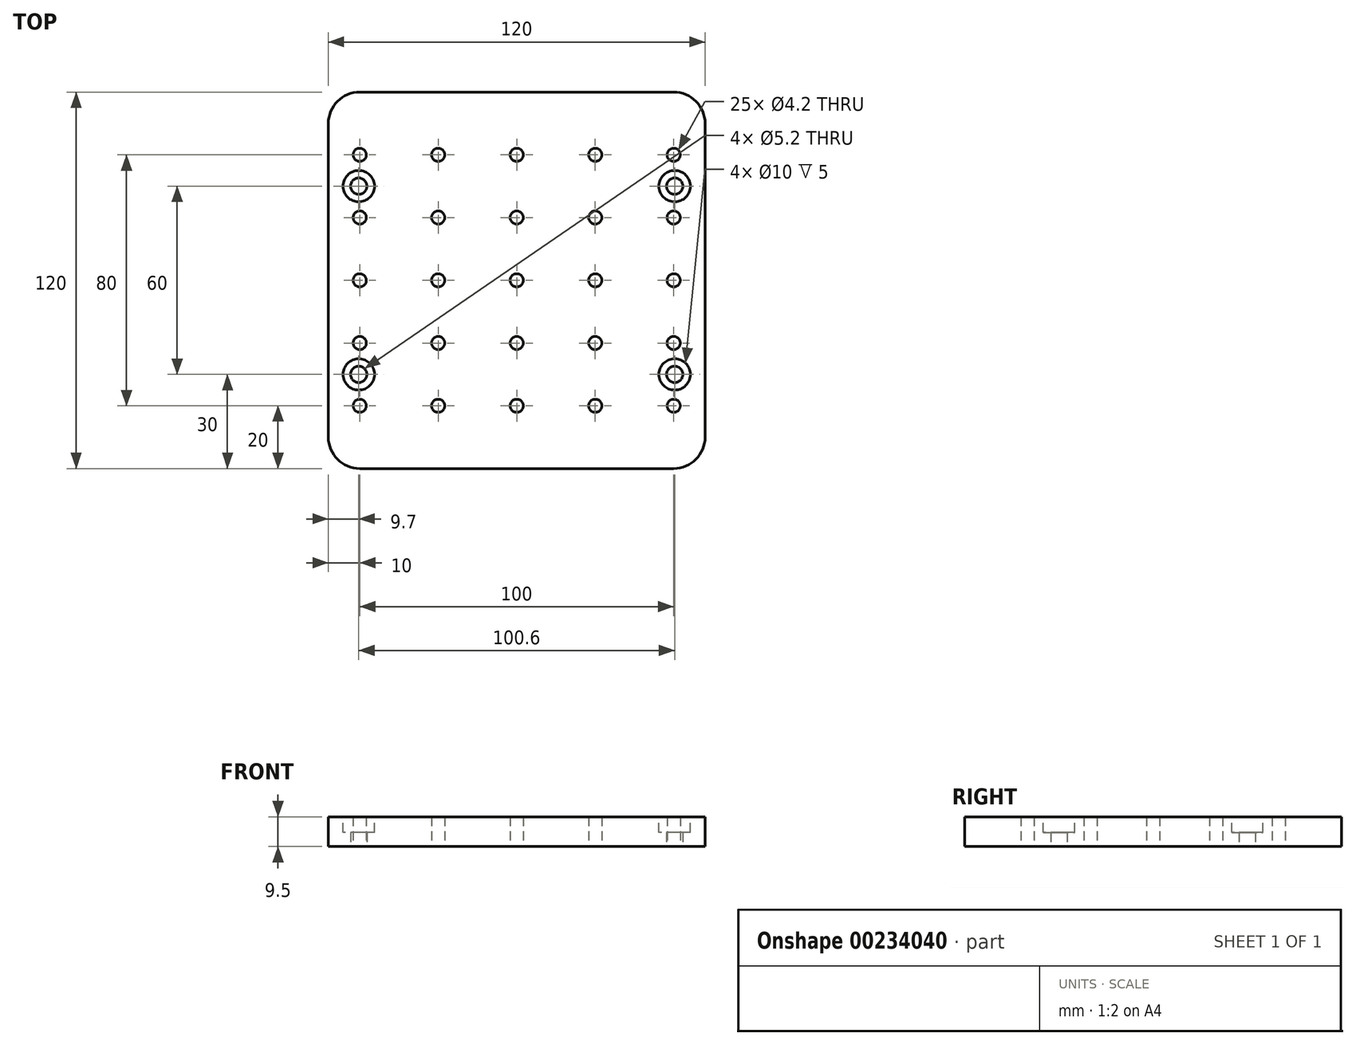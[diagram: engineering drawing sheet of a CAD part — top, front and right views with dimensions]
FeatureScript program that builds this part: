
annotation { "Feature Type Name" : "Feature", "Feature Type Description" : "" }
export const myFeature = defineFeature(function(context is Context, id is Id, definition is map)
    precondition{}
    {
        {
            var Q0;
            Q0=qCreatedBy(makeId("Top.planeOp"),FACE);
            var sketch = newSketch(context, id + "F0", { "sketchPlane" : qUnion([Q0])});
            skLineSegment(sketch, "E0.bottom", {"start": v(50, -60) * mm, "end": v(-50, -60) * mm});
            skLineSegment(sketch, "E0.top", {"start": v(50, 60) * mm, "end": v(-50, 60) * mm});
            skLineSegment(sketch, "E0.left", {"start": v(60, -50) * mm, "end": v(60, 50) * mm});
            skLineSegment(sketch, "E0.right", {"start": v(-60, -50) * mm, "end": v(-60, 50) * mm});
            skPoint(sketch, "E0.middle", {"position": v(0, 0) * mm});
            skPoint(sketch, "E1.visualSharp", {"position": v(-60, 60) * mm});
            skArc(sketch, "E1.filletArc", {"start": v(-50, 60) * mm, "mid": v(-57.07, 57.07) * mm, "end": v(-60, 50) * mm});
            skPoint(sketch, "E2.visualSharp", {"position": v(-60, -60) * mm});
            skArc(sketch, "E2.filletArc", {"start": v(-60, -50) * mm, "mid": v(-57.07, -57.07) * mm, "end": v(-50, -60) * mm});
            skPoint(sketch, "E3.visualSharp", {"position": v(60, -60) * mm});
            skArc(sketch, "E3.filletArc", {"start": v(50, -60) * mm, "mid": v(57.07, -57.07) * mm, "end": v(60, -50) * mm});
            skPoint(sketch, "E4.visualSharp", {"position": v(60, 60) * mm});
            skArc(sketch, "E4.filletArc", {"start": v(60, 50) * mm, "mid": v(57.07, 57.07) * mm, "end": v(50, 60) * mm});
            skLineSegment(sketch, "E5.bottom", {"start": v(50.3, -30) * mm, "end": v(-50.3, -30) * mm, "construction": true});
            skLineSegment(sketch, "E5.top", {"start": v(50.3, 30) * mm, "end": v(-50.3, 30) * mm, "construction": true});
            skLineSegment(sketch, "E5.left", {"start": v(50.3, -30) * mm, "end": v(50.3, 30) * mm, "construction": true});
            skLineSegment(sketch, "E5.right", {"start": v(-50.3, -30) * mm, "end": v(-50.3, 30) * mm, "construction": true});
            skCircle(sketch, "E6", {"center": v(-50.3, 30) * mm, "radius": 2.6 * mm});
            skCircle(sketch, "E7", {"center": v(50.3, 30) * mm, "radius": 2.6 * mm});
            skCircle(sketch, "E8", {"center": v(-50.3, -30) * mm, "radius": 2.6 * mm});
            skCircle(sketch, "E9", {"center": v(50.3, -30) * mm, "radius": 2.6 * mm});
            skCircle(sketch, "E10", {"center": v(0, 0) * mm, "radius": 2.1 * mm});
            skCircle(sketch, "E11.0.1.0", {"center": v(0, 20) * mm, "radius": 2.1 * mm});
            skCircle(sketch, "E11.0.2.0", {"center": v(0, 40) * mm, "radius": 2.1 * mm});
            skCircle(sketch, "E11.1.0.0", {"center": v(25, 0) * mm, "radius": 2.1 * mm});
            skCircle(sketch, "E11.1.1.0", {"center": v(25, 20) * mm, "radius": 2.1 * mm});
            skCircle(sketch, "E11.1.2.0", {"center": v(25, 40) * mm, "radius": 2.1 * mm});
            skCircle(sketch, "E11.2.0.0", {"center": v(50, 0) * mm, "radius": 2.1 * mm});
            skCircle(sketch, "E11.2.1.0", {"center": v(50, 20) * mm, "radius": 2.1 * mm});
            skCircle(sketch, "E11.2.2.0", {"center": v(50, 40) * mm, "radius": 2.1 * mm});
            skLineSegment(sketch, "E11.direction1", {"start": v(0, 0) * mm, "end": v(25, 0) * mm, "construction": true});
            skLineSegment(sketch, "E11.direction2", {"start": v(0, 0) * mm, "end": v(0, 20) * mm, "construction": true});
            skCircle(sketch, "E12.1.0.0", {"center": v(-25, 0) * mm, "radius": 2.1 * mm});
            skCircle(sketch, "E12.1.1.0", {"center": v(-25, 20) * mm, "radius": 2.1 * mm});
            skCircle(sketch, "E12.1.2.0", {"center": v(-25, 40) * mm, "radius": 2.1 * mm});
            skCircle(sketch, "E12.2.0.0", {"center": v(-50, 0) * mm, "radius": 2.1 * mm});
            skCircle(sketch, "E12.2.1.0", {"center": v(-50, 20) * mm, "radius": 2.1 * mm});
            skCircle(sketch, "E12.2.2.0", {"center": v(-50, 40) * mm, "radius": 2.1 * mm});
            skLineSegment(sketch, "E12.direction1", {"start": v(0, 0) * mm, "end": v(-25, 0) * mm, "construction": true});
            skCircle(sketch, "E13.0.1.0", {"center": v(50, -20) * mm, "radius": 2.1 * mm});
            skCircle(sketch, "E13.0.1.1", {"center": v(25, -20) * mm, "radius": 2.1 * mm});
            skCircle(sketch, "E13.0.1.2", {"center": v(0, -20) * mm, "radius": 2.1 * mm});
            skCircle(sketch, "E13.0.1.3", {"center": v(-25, -20) * mm, "radius": 2.1 * mm});
            skCircle(sketch, "E13.0.1.4", {"center": v(-50, -20) * mm, "radius": 2.1 * mm});
            skCircle(sketch, "E13.0.2.0", {"center": v(50, -40) * mm, "radius": 2.1 * mm});
            skCircle(sketch, "E13.0.2.1", {"center": v(25, -40) * mm, "radius": 2.1 * mm});
            skCircle(sketch, "E13.0.2.2", {"center": v(0, -40) * mm, "radius": 2.1 * mm});
            skCircle(sketch, "E13.0.2.3", {"center": v(-25, -40) * mm, "radius": 2.1 * mm});
            skCircle(sketch, "E13.0.2.4", {"center": v(-50, -40) * mm, "radius": 2.1 * mm});
            skLineSegment(sketch, "E13.direction1", {"start": v(-50, 0) * mm, "end": v(-25, 0) * mm, "construction": true});
            skLineSegment(sketch, "E13.direction2", {"start": v(-50, 0) * mm, "end": v(-50, -20) * mm, "construction": true});
            skSolve(sketch);
        }
        {
            var Q0;
            Q0=qSketchRegion(id+"F0",true);
            extrude(context, id + "F1", {"entities" : qUnion([Q0]), "depth" : 9.5 * mm});
        }
        {
            var Q0;
            Q0=makeQuery(id+"F1.opExtrude","CAP_FACE",FACE,{"disambiguationData":[OSD([sQuery(id+"F0.wireOp",EDGE,"E0.bottom"),sQuery(id+"F0.wireOp",EDGE,"E0.top"),sQuery(id+"F0.wireOp",EDGE,"E0.left"),sQuery(id+"F0.wireOp",EDGE,"E0.right"),sQuery(id+"F0.wireOp",EDGE,"E1.filletArc"),sQuery(id+"F0.wireOp",EDGE,"E2.filletArc"),sQuery(id+"F0.wireOp",EDGE,"E3.filletArc"),sQuery(id+"F0.wireOp",EDGE,"E4.filletArc"),sQuery(id+"F0.wireOp",EDGE,"E6"),sQuery(id+"F0.wireOp",EDGE,"E7"),sQuery(id+"F0.wireOp",EDGE,"E8"),sQuery(id+"F0.wireOp",EDGE,"E9"),sQuery(id+"F0.wireOp",EDGE,"E10"),sQuery(id+"F0.wireOp",EDGE,"E11.1.0.0"),sQuery(id+"F0.wireOp",EDGE,"E11.1.1.0"),sQuery(id+"F0.wireOp",EDGE,"E11.1.2.0"),sQuery(id+"F0.wireOp",EDGE,"E11.2.0.0"),sQuery(id+"F0.wireOp",EDGE,"E11.2.1.0"),sQuery(id+"F0.wireOp",EDGE,"E11.2.2.0"),sQuery(id+"F0.wireOp",EDGE,"E11.0.1.0"),sQuery(id+"F0.wireOp",EDGE,"E11.0.2.0"),sQuery(id+"F0.wireOp",EDGE,"E12.1.0.0"),sQuery(id+"F0.wireOp",EDGE,"E12.1.1.0"),sQuery(id+"F0.wireOp",EDGE,"E12.1.2.0"),sQuery(id+"F0.wireOp",EDGE,"E12.2.0.0"),sQuery(id+"F0.wireOp",EDGE,"E12.2.1.0"),sQuery(id+"F0.wireOp",EDGE,"E12.2.2.0"),sQuery(id+"F0.wireOp",EDGE,"E13.0.1.0"),sQuery(id+"F0.wireOp",EDGE,"E13.0.1.1"),sQuery(id+"F0.wireOp",EDGE,"E13.0.1.2"),sQuery(id+"F0.wireOp",EDGE,"E13.0.1.3"),sQuery(id+"F0.wireOp",EDGE,"E13.0.1.4"),sQuery(id+"F0.wireOp",EDGE,"E13.0.2.0"),sQuery(id+"F0.wireOp",EDGE,"E13.0.2.1"),sQuery(id+"F0.wireOp",EDGE,"E13.0.2.2"),sQuery(id+"F0.wireOp",EDGE,"E13.0.2.3"),sQuery(id+"F0.wireOp",EDGE,"E13.0.2.4")])],"isStart":false});
            var sketch = newSketch(context, id + "F2", { "sketchPlane" : qUnion([Q0])});
            skCircle(sketch, "E14", {"center": v(-50.3, 30) * mm, "radius": 5 * mm});
            skCircle(sketch, "E15", {"center": v(-50.3, -30) * mm, "radius": 5 * mm});
            skCircle(sketch, "E16", {"center": v(50.3, 30) * mm, "radius": 5 * mm});
            skCircle(sketch, "E17", {"center": v(50.3, -30) * mm, "radius": 5 * mm});
            skSolve(sketch);
        }
        {
            var Q0;
            Q0 = qSketchRegion(id + "F2", true);
            extrude(context, id + "F3", {"entities" : qUnion([Q0]), "operationType" : NewBodyOperationType.REMOVE, "oppositeDirection" : true, "depth" : 5 * mm});
        }
    });
